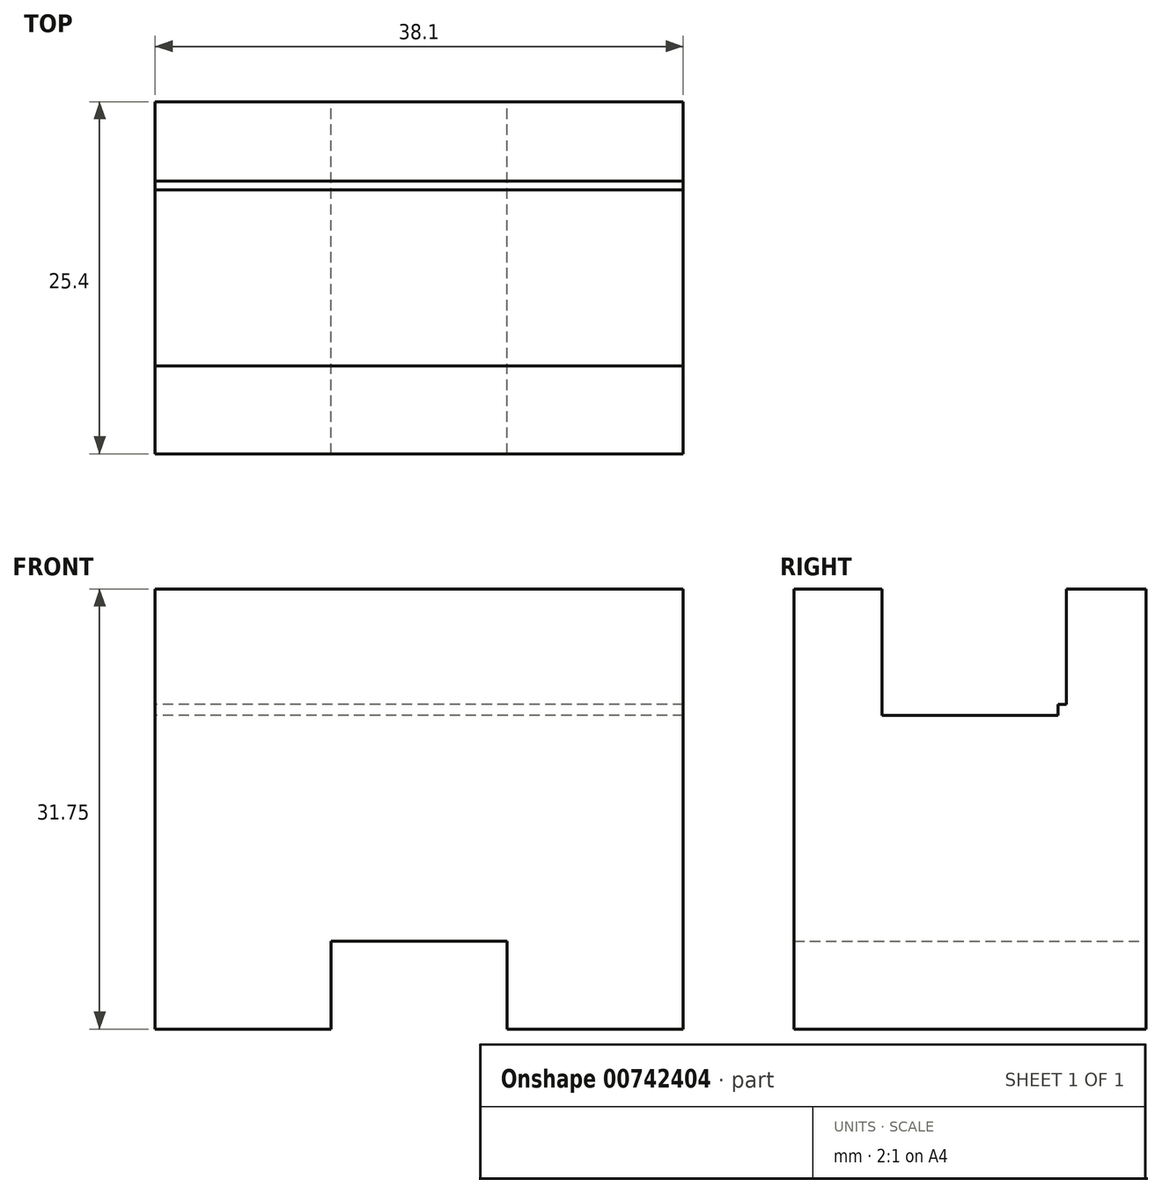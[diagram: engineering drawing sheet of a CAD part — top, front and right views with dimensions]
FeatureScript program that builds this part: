
annotation { "Feature Type Name" : "Feature", "Feature Type Description" : "" }
export const myFeature = defineFeature(function(context is Context, id is Id, definition is map)
    precondition{}
    {
        {
            var Q0;
            Q0=qCreatedBy(makeId("Front.planeOp"),FACE);
            var sketch = newSketch(context, id + "F0", { "sketchPlane" : qUnion([Q0])});
            skLineSegment(sketch, "E0", {"start": v(0, 0) * mm, "end": v(38.1, 0) * mm});
            skLineSegment(sketch, "E1", {"start": v(38.1, 31.75) * mm, "end": v(0, 31.75) * mm});
            skLineSegment(sketch, "E2", {"start": v(0, 31.75) * mm, "end": v(0, 0) * mm});
            skLineSegment(sketch, "E3", {"start": v(38.1, 31.75) * mm, "end": v(38.1, 0) * mm});
            skSolve(sketch);
        }
        {
            var Q0;
            Q0=makeQuery(id+"F0.imprint","IMPRINT",FACE,{"disambiguationData":[TD([[makeQuery(id+"F0.imprint","IMPRINT",EDGE,{"derivedFrom":sQuery(id+"F0.wireOp",EDGE,"E0")}),1.0]])]});
            extrude(context, id + "F1", {"entities" : qUnion([Q0]), "depth" : 25.4 * mm, "offsetDistance" : 25.4 * mm});
        }
        {
            var Q0;
            Q0=qCreatedBy(makeId("Front.planeOp"),FACE);
            var sketch = newSketch(context, id + "F2", { "sketchPlane" : qUnion([Q0])});
            skLineSegment(sketch, "E4", {"start": v(25.4, 0) * mm, "end": v(25.4, 6.35) * mm});
            skLineSegment(sketch, "E5", {"start": v(25.4, 6.35) * mm, "end": v(12.7, 6.35) * mm});
            skLineSegment(sketch, "E6", {"start": v(12.7, 6.35) * mm, "end": v(12.7, 0) * mm});
            skLineSegment(sketch, "E7", {"start": v(12.7, 0) * mm, "end": v(25.4, 0) * mm});
            skSolve(sketch);
        }
        {
            var Q0;
            Q0=makeQuery(id+"F2.imprint","IMPRINT",FACE,{"disambiguationData":[TD([[makeQuery(id+"F2.imprint","IMPRINT",EDGE,{"derivedFrom":sQuery(id+"F2.wireOp",EDGE,"E4")}),1.0]])]});
            extrude(context, id + "F3", {"entities" : qUnion([Q0]), "operationType" : NewBodyOperationType.REMOVE, "endBound" : BoundingType.THROUGH_ALL, "depth" : 25.4 * mm, "offsetDistance" : 25.4 * mm});
        }
        {
            var Q0;
            Q0=qCreatedBy(makeId("Right.planeOp"),FACE);
            var sketch = newSketch(context, id + "F4", { "sketchPlane" : qUnion([Q0])});
            skLineSegment(sketch, "E8", {"start": v(-19.05, 31.95) * mm, "end": v(-19.05, 22.63) * mm});
            skLineSegment(sketch, "E9", {"start": v(-19.05, 22.63) * mm, "end": v(-6.35, 22.63) * mm});
            skLineSegment(sketch, "E10", {"start": v(-6.35, 22.63) * mm, "end": v(-6.35, 31.66) * mm});
            skLineSegment(sketch, "E11", {"start": v(-6.35, 31.66) * mm, "end": v(-19.05, 31.95) * mm});
            skSolve(sketch);
        }
        {
            var Q0;
            Q0 = qSketchRegion(id + "F4", true);
            extrude(context, id + "F5", {"entities" : qUnion([Q0]), "operationType" : NewBodyOperationType.REMOVE, "endBound" : BoundingType.THROUGH_ALL, "depth" : 25.4 * mm, "offsetDistance" : 25.4 * mm});
        }
        {
            var Q0;
            Q0=qCreatedBy(makeId("Right.planeOp"),FACE);
            var sketch = newSketch(context, id + "F6", { "sketchPlane" : qUnion([Q0])});
            skLineSegment(sketch, "E12", {"start": v(-10.39, 32.4) * mm, "end": v(-10.39, 23.41) * mm});
            skLineSegment(sketch, "E13", {"start": v(-10.39, 23.41) * mm, "end": v(-5.74, 23.41) * mm});
            skLineSegment(sketch, "E14", {"start": v(-5.74, 23.41) * mm, "end": v(-5.74, 32.4) * mm});
            skLineSegment(sketch, "E15", {"start": v(-5.74, 32.4) * mm, "end": v(-10.39, 32.4) * mm});
            skSolve(sketch);
        }
        {
            var Q0;
            Q0 = qSketchRegion(id + "F6", true);
            extrude(context, id + "F7", {"entities" : qUnion([Q0]), "operationType" : NewBodyOperationType.REMOVE, "endBound" : BoundingType.THROUGH_ALL, "depth" : 25.4 * mm, "offsetDistance" : 25.4 * mm});
        }
    });
